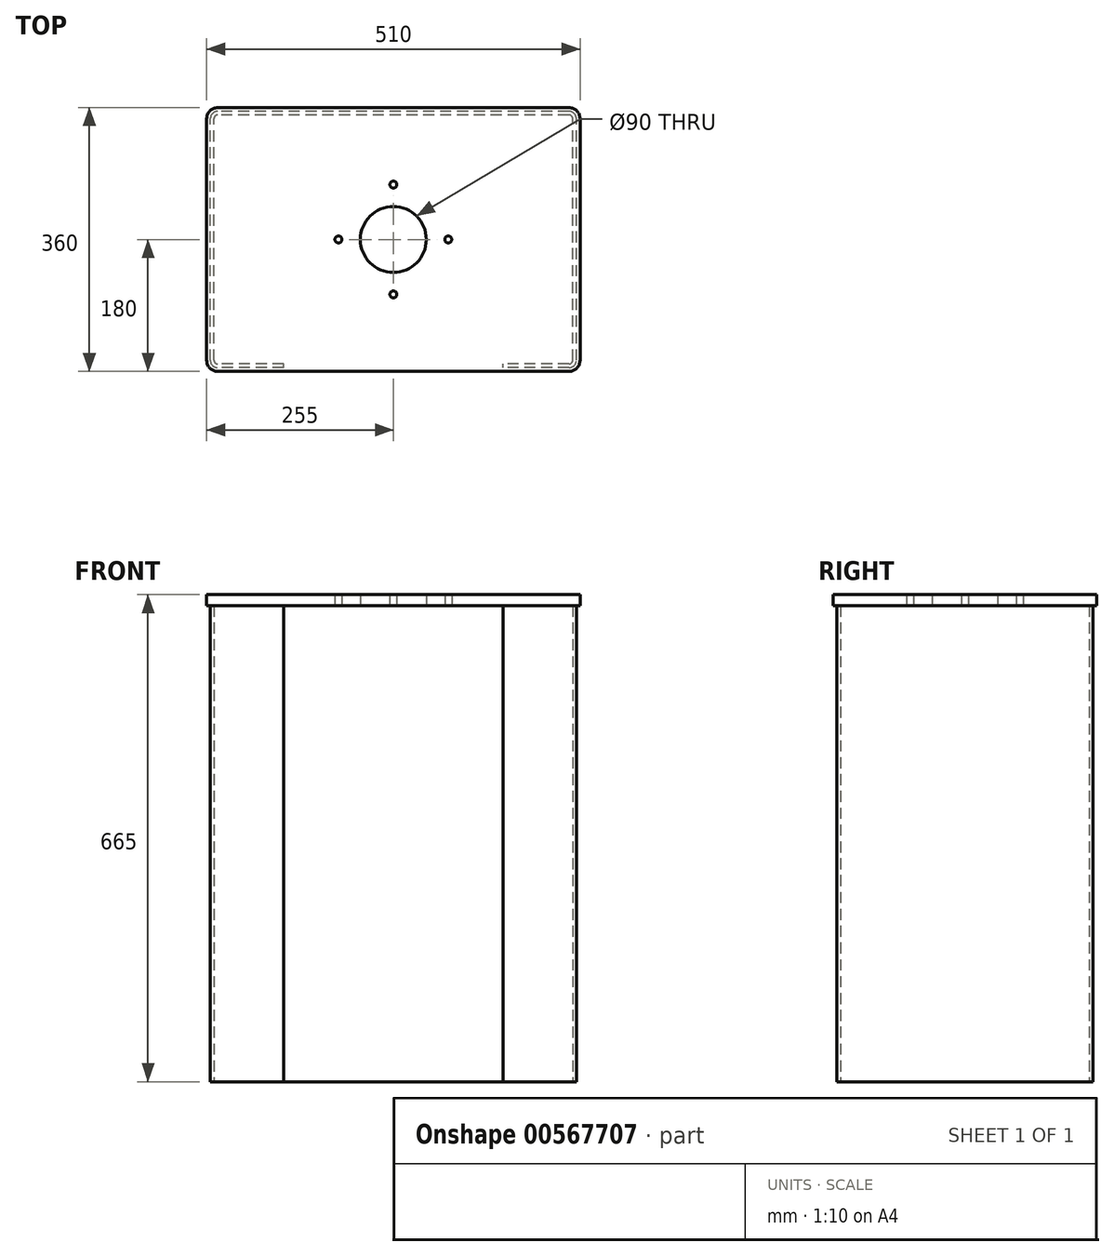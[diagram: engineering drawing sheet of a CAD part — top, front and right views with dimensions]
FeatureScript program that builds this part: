
annotation { "Feature Type Name" : "Feature", "Feature Type Description" : "" }
export const myFeature = defineFeature(function(context is Context, id is Id, definition is map)
    precondition{}
    {
        {
            var Q0;
            Q0=qCreatedBy(makeId("Top.planeOp"),FACE);
            var sketch = newSketch(context, id + "F0", { "sketchPlane" : qUnion([Q0])});
            skLineSegment(sketch, "E0.bottom", {"start": v(240, -175) * mm, "end": v(150, -175) * mm});
            skLineSegment(sketch, "E0.top", {"start": v(240, 175) * mm, "end": v(-240, 175) * mm});
            skLineSegment(sketch, "E0.left", {"start": v(250, -165) * mm, "end": v(250, 165) * mm});
            skLineSegment(sketch, "E0.right", {"start": v(-250, -165) * mm, "end": v(-250, 165) * mm});
            skPoint(sketch, "E0.middle", {"position": v(0, 0) * mm});
            skLineSegment(sketch, "E1.0", {"start": v(240, 170) * mm, "end": v(-240, 170) * mm});
            skLineSegment(sketch, "E2.0", {"start": v(245, -165) * mm, "end": v(245, 165) * mm});
            skLineSegment(sketch, "E3.0", {"start": v(240, -170) * mm, "end": v(150, -170) * mm});
            skLineSegment(sketch, "E4.0", {"start": v(-245, -165) * mm, "end": v(-245, 165) * mm});
            skArc(sketch, "E5.filletArc", {"start": v(-240, 170) * mm, "mid": v(-243.54, 168.54) * mm, "end": v(-245, 165) * mm});
            skArc(sketch, "E6.filletArc", {"start": v(245, 165) * mm, "mid": v(243.54, 168.54) * mm, "end": v(240, 170) * mm});
            skArc(sketch, "E7.filletArc", {"start": v(240, -170) * mm, "mid": v(243.54, -168.54) * mm, "end": v(245, -165) * mm});
            skArc(sketch, "E8.filletArc", {"start": v(-245, -165) * mm, "mid": v(-243.54, -168.54) * mm, "end": v(-240, -170) * mm});
            skPoint(sketch, "E9.visualSharp", {"position": v(-250, 175) * mm});
            skArc(sketch, "E9.filletArc", {"start": v(-240, 175) * mm, "mid": v(-247.07, 172.07) * mm, "end": v(-250, 165) * mm});
            skPoint(sketch, "E10.visualSharp", {"position": v(250, 175) * mm});
            skArc(sketch, "E10.filletArc", {"start": v(250, 165) * mm, "mid": v(247.07, 172.07) * mm, "end": v(240, 175) * mm});
            skPoint(sketch, "E11.visualSharp", {"position": v(250, -175) * mm});
            skArc(sketch, "E11.filletArc", {"start": v(240, -175) * mm, "mid": v(247.07, -172.07) * mm, "end": v(250, -165) * mm});
            skPoint(sketch, "E12.visualSharp", {"position": v(-250, -175) * mm});
            skArc(sketch, "E12.filletArc", {"start": v(-250, -165) * mm, "mid": v(-247.07, -172.07) * mm, "end": v(-240, -175) * mm});
            skLineSegment(sketch, "E13.0", {"start": v(150, -175) * mm, "end": v(150, -170) * mm});
            skLineSegment(sketch, "E14.0", {"start": v(-150, -175) * mm, "end": v(-150, -170) * mm});
            skLineSegment(sketch, "E15.trimOffspring", {"start": v(-150, -170) * mm, "end": v(-240, -170) * mm});
            skLineSegment(sketch, "E16.trimOffspring", {"start": v(-150, -175) * mm, "end": v(-240, -175) * mm});
            skSolve(sketch);
        }
        {
            var Q0;
            Q0=makeQuery(id+"F0.imprint","IMPRINT",FACE,{"disambiguationData":[TD([[makeQuery(id+"F0.imprint","IMPRINT",EDGE,{"derivedFrom":sQuery(id+"F0.wireOp",EDGE,"E0.bottom")}),-1.0]])]});
            extrude(context, id + "F1", {"entities" : qUnion([Q0]), "depth" : 650 * mm, "offsetDistance" : 25 * mm});
        }
        {
            var Q0;
            Q0=makeQuery(id+"F1.opExtrude","CAP_FACE",FACE,{"disambiguationData":[OSD([sQuery(id+"F0.wireOp",EDGE,"E0.bottom"),sQuery(id+"F0.wireOp",EDGE,"E0.top"),sQuery(id+"F0.wireOp",EDGE,"E0.left"),sQuery(id+"F0.wireOp",EDGE,"E0.right"),sQuery(id+"F0.wireOp",EDGE,"E1.0"),sQuery(id+"F0.wireOp",EDGE,"E2.0"),sQuery(id+"F0.wireOp",EDGE,"E3.0"),sQuery(id+"F0.wireOp",EDGE,"E4.0"),sQuery(id+"F0.wireOp",EDGE,"E5.filletArc"),sQuery(id+"F0.wireOp",EDGE,"E6.filletArc"),sQuery(id+"F0.wireOp",EDGE,"E7.filletArc"),sQuery(id+"F0.wireOp",EDGE,"E8.filletArc"),sQuery(id+"F0.wireOp",EDGE,"E9.filletArc"),sQuery(id+"F0.wireOp",EDGE,"E10.filletArc"),sQuery(id+"F0.wireOp",EDGE,"E11.filletArc"),sQuery(id+"F0.wireOp",EDGE,"E12.filletArc"),sQuery(id+"F0.wireOp",EDGE,"E13.0"),sQuery(id+"F0.wireOp",EDGE,"E14.0"),sQuery(id+"F0.wireOp",EDGE,"E15.trimOffspring"),sQuery(id+"F0.wireOp",EDGE,"E16.trimOffspring")])],"isStart":false});
            var sketch = newSketch(context, id + "F2", { "sketchPlane" : qUnion([Q0])});
            skArc(sketch, "E17.0", {"start": v(-240, 175) * mm, "mid": v(-247.07, 172.07) * mm, "end": v(-250, 165) * mm, "construction": true});
            skArc(sketch, "E18.0", {"start": v(250, 165) * mm, "mid": v(247.07, 172.07) * mm, "end": v(240, 175) * mm});
            skLineSegment(sketch, "E19.0.0", {"start": v(-150, -175) * mm, "end": v(-150, -170) * mm, "construction": true});
            skArc(sketch, "E19.0.4", {"start": v(-245, 165) * mm, "mid": v(-243.54, 168.54) * mm, "end": v(-240, 170) * mm, "construction": true});
            skArc(sketch, "E19.0.6", {"start": v(240, 170) * mm, "mid": v(243.54, 168.54) * mm, "end": v(245, 165) * mm, "construction": true});
            skLineSegment(sketch, "E19.0.7", {"start": v(245, 165) * mm, "end": v(245, -165) * mm});
            skArc(sketch, "E19.0.8", {"start": v(245, -165) * mm, "mid": v(243.54, -168.54) * mm, "end": v(240, -170) * mm});
            skLineSegment(sketch, "E19.0.9", {"start": v(240, -170) * mm, "end": v(150, -170) * mm, "construction": true});
            skLineSegment(sketch, "E19.0.10", {"start": v(150, -170) * mm, "end": v(150, -175) * mm});
            skLineSegment(sketch, "E19.0.11", {"start": v(150, -175) * mm, "end": v(240, -175) * mm});
            skArc(sketch, "E19.0.12", {"start": v(240, -175) * mm, "mid": v(247.07, -172.07) * mm, "end": v(250, -165) * mm, "construction": true});
            skLineSegment(sketch, "E19.0.13", {"start": v(250, -165) * mm, "end": v(250, 165) * mm, "construction": true});
            skArc(sketch, "E19.0.14", {"start": v(250, 165) * mm, "mid": v(247.07, 172.07) * mm, "end": v(240, 175) * mm, "construction": true});
            skArc(sketch, "E19.0.16", {"start": v(-240, 175) * mm, "mid": v(-247.07, 172.07) * mm, "end": v(-250, 165) * mm});
            skLineSegment(sketch, "E20.0.0", {"start": v(-150, -175) * mm, "end": v(-150, -170) * mm});
            skArc(sketch, "E20.0.4", {"start": v(-245, 165) * mm, "mid": v(-243.54, 168.54) * mm, "end": v(-240, 170) * mm});
            skArc(sketch, "E20.0.6", {"start": v(240, 170) * mm, "mid": v(243.54, 168.54) * mm, "end": v(245, 165) * mm});
            skLineSegment(sketch, "E20.0.7", {"start": v(245, 165) * mm, "end": v(245, -165) * mm, "construction": true});
            skLineSegment(sketch, "E20.0.9", {"start": v(240, -170) * mm, "end": v(150, -170) * mm});
            skLineSegment(sketch, "E20.0.10", {"start": v(150, -170) * mm, "end": v(150, -175) * mm, "construction": true});
            skLineSegment(sketch, "E20.0.11", {"start": v(150, -175) * mm, "end": v(240, -175) * mm, "construction": true});
            skArc(sketch, "E20.0.12", {"start": v(240, -175) * mm, "mid": v(247.07, -172.07) * mm, "end": v(250, -165) * mm});
            skLineSegment(sketch, "E20.0.13", {"start": v(250, -165) * mm, "end": v(250, 165) * mm});
            skArc(sketch, "E21.0", {"start": v(-240, 180) * mm, "mid": v(-250.6, 175.6) * mm, "end": v(-255, 165) * mm});
            skLineSegment(sketch, "E22.0", {"start": v(240, 180) * mm, "end": v(-240, 180) * mm});
            skArc(sketch, "E23.0", {"start": v(255, 165) * mm, "mid": v(250.6, 175.6) * mm, "end": v(240, 180) * mm});
            skLineSegment(sketch, "E24.0", {"start": v(255, -165) * mm, "end": v(255, 165) * mm});
            skArc(sketch, "E25.0", {"start": v(240, -180) * mm, "mid": v(250.6, -175.6) * mm, "end": v(255, -165) * mm});
            skLineSegment(sketch, "E26.0", {"start": v(150, -180) * mm, "end": v(240, -180) * mm});
            skLineSegment(sketch, "E27.0", {"start": v(-240, -180) * mm, "end": v(-150, -180) * mm});
            skArc(sketch, "E28.0", {"start": v(-255, -165) * mm, "mid": v(-250.6, -175.6) * mm, "end": v(-240, -180) * mm});
            skLineSegment(sketch, "E29.0", {"start": v(-255, 165) * mm, "end": v(-255, -165) * mm});
            skLineSegment(sketch, "E30", {"start": v(-150, -180) * mm, "end": v(150, -180) * mm});
            skCircle(sketch, "E31", {"center": v(0, 0) * mm, "radius": 45 * mm});
            skCircle(sketch, "E32", {"center": v(0, 0) * mm, "radius": 75 * mm, "construction": true});
            skCircle(sketch, "E33", {"center": v(-75, 0) * mm, "radius": 4.75 * mm});
            skCircle(sketch, "E34.1.0", {"center": v(0, -75) * mm, "radius": 4.75 * mm});
            skCircle(sketch, "E34.2.0", {"center": v(75, 0) * mm, "radius": 4.75 * mm});
            skCircle(sketch, "E35.1.3.0", {"center": v(0, 75) * mm, "radius": 4.75 * mm});
            skSolve(sketch);
        }
        {
            var Q0;
            Q0=makeQuery(id+"F2.imprint","IMPRINT",FACE,{"disambiguationData":[TD([[makeQuery(id+"F2.imprint","IMPRINT",EDGE,{"derivedFrom":sQuery(id+"F2.wireOp",EDGE,"E19.0.7")}),1.0]])]});
            var Q1;
            Q1=makeQuery(id+"F2.imprint","IMPRINT",FACE,{"disambiguationData":[TD([[makeQuery(id+"F2.imprint","IMPRINT",EDGE,{"derivedFrom":sQuery(id+"F2.wireOp",EDGE,"E19.0.7")}),-1.0]])]});
            var Q2;
            Q2=sQuery(id+"F2.wireOp",EDGE,"E30");
            var Q3;
            Q3=sQuery(id+"F2.wireOp",EDGE,"E26.0");
            var Q4;
            Q4=sQuery(id+"F2.wireOp",EDGE,"E25.0");
            var Q5;
            Q5=sQuery(id+"F2.wireOp",EDGE,"E24.0");
            var Q6;
            Q6=sQuery(id+"F2.wireOp",EDGE,"E22.0");
            var Q7;
            Q7=sQuery(id+"F2.wireOp",EDGE,"E23.0");
            var Q8;
            Q8=sQuery(id+"F2.wireOp",EDGE,"E21.0");
            var Q9;
            Q9=sQuery(id+"F2.wireOp",EDGE,"E29.0");
            var Q10;
            Q10=sQuery(id+"F2.wireOp",EDGE,"E28.0");
            var Q11;
            Q11=sQuery(id+"F2.wireOp",EDGE,"E27.0");
            extrude(context, id + "F3", {"entities" : qUnion([Q0, Q1]), "surfaceEntities" : qUnion([Q2, Q3, Q4, Q5, Q6, Q7, Q8, Q9, Q10, Q11]), "depth" : 15 * mm, "offsetDistance" : 25 * mm});
        }
    });
